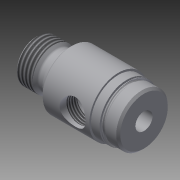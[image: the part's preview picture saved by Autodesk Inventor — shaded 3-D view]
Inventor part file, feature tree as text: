
AUTODESK INVENTOR PART (.ipt)
format: ipt  version: 2014 SP2 (Build 180246200, 246)  size: 272,384 bytes
history: native  units: in
note: dims shown in document units (in); Inventor stores cm internally (conversion verified against a paired STEP export)
features: other x119, sketch x6, revolve x5, thread x2, hole x1
ambient origin geometry x8: Origin, YZ Plane, XZ Plane, XY Plane, X Axis, Y Axis, Z Axis, Center Point
bodies: Solid1 (feature_tree)
feature tree (133):
  revolve  "Revolution1"  [1 undecoded]
  thread  "Thread1"  [1 undecoded]
  revolve  "Revolution2"  Angle=360.0deg
  hole  "Hole1"  [1 undecoded]
  revolve  "Revolution3"  [1 undecoded]
  revolve  "Revolution4"  [1 undecoded]
  thread  "Thread2"  [1 undecoded]
  revolve  "Revolution5"  [1 undecoded]
  other  "dp1_XY"
  other  "dp1_YZ"
  other  "dp1_ZX"
  other  "dp1_X"
  other  "dp1_Y"
  other  "dp1_Z"
  other  "dp1_Center"
  other  "dp2_XY"
  other  "dp2_YZ"
  other  "dp2_ZX"
  other  "dp2_X"
  other  "dp2_Y"
  other  "dp2_Z"
  other  "dp2_Center"
  other  "hh_XY"
  other  "hh_YZ"
  other  "hh_ZX"
  other  "hh_X"
  other  "hh_Y"
  other  "hh_Z"
  other  "hh_Center"
  other  "port_XY"
  other  "port_YZ"
  other  "port_ZX"
  other  "port_X"
  other  "port_Y"
  other  "port_Z"
  other  "port_Center"
  other  "rod_guide_XY"
  other  "rod_guide_YZ"
  other  "rod_guide_ZX"
  other  "rod_guide_X"
  other  "rod_guide_Y"
  other  "rod_guide_Z"
  other  "rod_guide_Center"
  other  "s1_XY"
  other  "s1_YZ"
  other  "s1_ZX"
  other  "s1_X"
  other  "s1_Y"
  other  "s1_Z"
  other  "s1_Center"
  other  "s2_XY"
  other  "s2_YZ"
  other  "s2_ZX"
  other  "s2_X"
  other  "s2_Y"
  other  "s2_Z"
  other  "s2_Center"
  other  "t1_XY"
  other  "t1_YZ"
  other  "t1_ZX"
  other  "t1_X"
  other  "t1_Y"
  other  "t1_Z"
  other  "t1_Center"
  other  "t111_XY"
  other  "t111_YZ"
  other  "t111_ZX"
  other  "t111_X"
  other  "t111_Y"
  other  "t111_Z"
  other  "t111_Center"
  other  "to_foot_bracket_XY"
  other  "to_foot_bracket_YZ"
  other  "to_foot_bracket_ZX"
  other  "to_foot_bracket_X"
  other  "to_foot_bracket_Y"
  other  "to_foot_bracket_Z"
  other  "to_foot_bracket_Center"
  other  "to_nut_XY"
  other  "to_nut_YZ"
  other  "to_nut_ZX"
  other  "to_nut_X"
  other  "to_nut_Y"
  other  "to_nut_Z"
  other  "to_nut_Center"
  other  "to_rod_XY"
  other  "to_rod_YZ"
  other  "to_rod_ZX"
  other  "to_rod_X"
  other  "to_rod_Y"
  other  "to_rod_Z"
  other  "to_rod_Center"
  other  "to_screw_XY"
  other  "to_screw_YZ"
  other  "to_screw_ZX"
  other  "to_screw_X"
  other  "to_screw_Y"
  other  "to_screw_Z"
  other  "to_screw_Center"
  other  "to_trunnion_brackets_XY"
  other  "to_trunnion_brackets_YZ"
  other  "to_trunnion_brackets_ZX"
  other  "to_trunnion_brackets_X"
  other  "to_trunnion_brackets_Y"
  other  "to_trunnion_brackets_Z"
  other  "to_trunnion_brackets_Center"
  other  "to_trunnion_brackets1_XY"
  other  "to_trunnion_brackets1_YZ"
  other  "to_trunnion_brackets1_ZX"
  other  "to_trunnion_brackets1_X"
  other  "to_trunnion_brackets1_Y"
  other  "to_trunnion_brackets1_Z"
  other  "to_trunnion_brackets1_Center"
  other  "to_trunnion_brackets2_XY"
  other  "to_trunnion_brackets2_YZ"
  other  "to_trunnion_brackets2_ZX"
  other  "to_trunnion_brackets2_X"
  other  "to_trunnion_brackets2_Y"
  other  "to_trunnion_brackets2_Z"
  other  "to_trunnion_brackets2_Center"
  other  "to_tube_XY"
  other  "to_tube_YZ"
  other  "to_tube_ZX"
  other  "to_tube_X"
  other  "to_tube_Y"
  other  "to_tube_Z"
  other  "to_tube_Center"
  sketch  "Sketch_2"  dims[d0=360.0deg d1=0.23in d2=0.0in d3=360.0deg]
  sketch  "Sketch_3"  dims[d4=0.2535in d5=0.75in d6=0.2735in d7=0.25in d8=90.0deg d9=1.594in d10=0.0in d11=360.0deg]
  sketch  "Sketch3"  dims[d12=360.0deg d13=0.1501in d14=0.0in]
  sketch  "Sketch_10"  dims[d15=360.0deg]
  sketch  "Sketch_40"  dims[d16=0.0in d17=0.0in d18=0.0in d19=0.0in d20=0.0in]
  sketch  "Sketch_47"
note: 7 required parameter values undecoded (feature->parameter linkage not recoverable at this tier; creation-order binding heuristic only, values carry confidence <= 0.55)